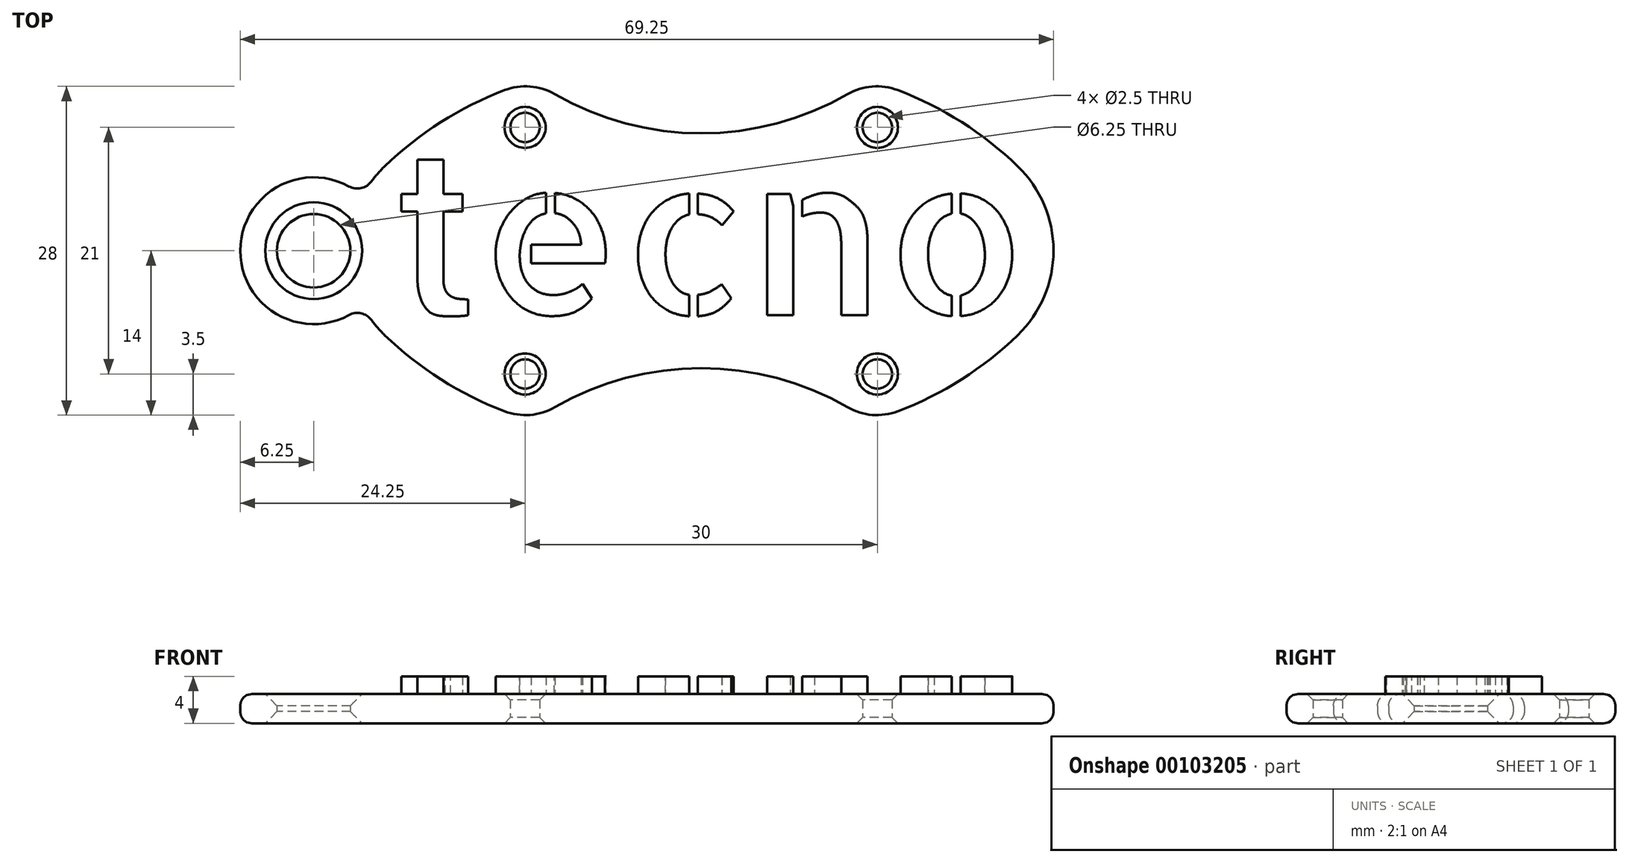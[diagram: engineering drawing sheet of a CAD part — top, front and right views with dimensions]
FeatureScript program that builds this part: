
annotation { "Feature Type Name" : "Feature", "Feature Type Description" : "" }
export const myFeature = defineFeature(function(context is Context, id is Id, definition is map)
    precondition{}
    {
        {
            var Q0;
            Q0=qCreatedBy(makeId("Top.planeOp"),FACE);
            var sketch = newSketch(context, id + "F0", { "sketchPlane" : qUnion([Q0])});
            skArc(sketch, "E0", {"start": v(-53.9, 14.37) * mm, "mid": v(-55.07, 13.14) * mm, "end": v(-56.13, 11.82) * mm});
            skArc(sketch, "E1.MirrorC", {"start": v(53.9, 14.37) * mm, "mid": v(60, 0) * mm, "end": v(53.9, -14.37) * mm});
            skArc(sketch, "E2", {"start": v(-53.9, -14.37) * mm, "mid": v(-44.35, -21.9) * mm, "end": v(-33.48, -27.35) * mm});
            skArc(sketch, "E3", {"start": v(24.94, -26.66) * mm, "mid": v(0, -20) * mm, "end": v(-24.94, -26.66) * mm});
            skArc(sketch, "E4", {"start": v(-33.48, -27.35) * mm, "mid": v(-29.13, -27.97) * mm, "end": v(-24.94, -26.66) * mm});
            skPoint(sketch, "E5.orphan", {"position": v(0, -30) * mm});
            skArc(sketch, "E6.MirrorCS", {"start": v(33.48, -27.35) * mm, "mid": v(29.13, -27.97) * mm, "end": v(24.94, -26.66) * mm});
            skArc(sketch, "E7.MirrorCS", {"start": v(53.9, -14.37) * mm, "mid": v(44.35, -21.9) * mm, "end": v(33.48, -27.35) * mm});
            skArc(sketch, "E8.MirrorCS", {"start": v(53.9, 14.37) * mm, "mid": v(44.35, 21.9) * mm, "end": v(33.48, 27.35) * mm});
            skArc(sketch, "E9.MirrorCS", {"start": v(33.48, 27.35) * mm, "mid": v(29.13, 27.97) * mm, "end": v(24.94, 26.66) * mm});
            skArc(sketch, "E10.MirrorCS", {"start": v(24.94, 26.66) * mm, "mid": v(0, 20) * mm, "end": v(-24.94, 26.66) * mm});
            skArc(sketch, "E11.MirrorCS", {"start": v(-33.48, 27.35) * mm, "mid": v(-29.13, 27.97) * mm, "end": v(-24.94, 26.66) * mm});
            skArc(sketch, "E12.MirrorCS", {"start": v(-53.9, 14.37) * mm, "mid": v(-44.35, 21.9) * mm, "end": v(-33.48, 27.35) * mm});
            skArc(sketch, "E13", {"start": v(-60, 10.96) * mm, "mid": v(-78.5, 0) * mm, "end": v(-60, -10.96) * mm});
            skArc(sketch, "E14.trimOffspring", {"start": v(-56.13, -11.82) * mm, "mid": v(-55.07, -13.14) * mm, "end": v(-53.9, -14.37) * mm});
            skArc(sketch, "E15", {"start": v(-60, 10.96) * mm, "mid": v(-57.9, 10.67) * mm, "end": v(-56.13, 11.82) * mm});
            skArc(sketch, "E16.MirrorCS", {"start": v(-60, -10.96) * mm, "mid": v(-57.9, -10.67) * mm, "end": v(-56.13, -11.82) * mm});
            skCircle(sketch, "E17", {"center": v(-66, 0) * mm, "radius": 6.25 * mm});
            skCircle(sketch, "E18", {"center": v(-30, -21) * mm, "radius": 2.5 * mm});
            skText(sketch, "E19", { "text": "tecno", "fontName": "AllertaStencil-Regular.ttf"});
            skCircle(sketch, "E20.MirrorC", {"center": v(-30, 21) * mm, "radius": 2.5 * mm});
            skCircle(sketch, "E21.MirrorC", {"center": v(30, 21) * mm, "radius": 2.5 * mm});
            skCircle(sketch, "E22.MirrorC", {"center": v(30, -21) * mm, "radius": 2.5 * mm});
            const initialGuessF0  = {"E19": [-0.05296, -0.011, 1, 0, 0.027]};
            skSetInitialGuess(sketch, initialGuessF0);
            skSolve(sketch);
        }
        {
            var Q0;
            Q0=makeQuery(id+"F0.imprint","IMPRINT",FACE,{"disambiguationData":[TD([[makeQuery(id+"F0.imprint","IMPRINT",EDGE,{"derivedFrom":sQuery(id+"F0.wireOp",EDGE,"E0")}),1.0]])]});
            extrude(context, id + "F1", {"entities" : qUnion([Q0]), "depth" : 5 * mm});
        }
        {
            var Q0;
            Q0=makeQuery(id+"F1.opExtrude","CAP_EDGE",EDGE,{"disambiguationData":[OSD([sQuery(id+"F0.wireOp",EDGE,"3ecefedf-33f3-4cd3-ba5f-a2dd52aaf8ab1.MirrorC")])],"isStart":true});
            var Q1;
            Q1=makeQuery(id+"F1.opExtrude","CAP_EDGE",EDGE,{"disambiguationData":[OSD([sQuery(id+"F0.wireOp",EDGE,"E20.MirrorC")])],"isStart":false});
            var Q2;
            Q2=makeQuery(id+"F1.opExtrude","CAP_EDGE",EDGE,{"disambiguationData":[OSD([sQuery(id+"F0.wireOp",EDGE,"E18")])],"isStart":false});
            var Q3;
            Q3=makeQuery(id+"F1.opExtrude","CAP_EDGE",EDGE,{"disambiguationData":[OSD([sQuery(id+"F0.wireOp",EDGE,"E22.MirrorC")])],"isStart":false});
            var Q4;
            Q4=makeQuery(id+"F1.opExtrude","CAP_EDGE",EDGE,{"disambiguationData":[OSD([sQuery(id+"F0.wireOp",EDGE,"E21.MirrorC")])],"isStart":false});
            var Q5;
            Q5=makeQuery(id+"F1.opExtrude","CAP_EDGE",EDGE,{"disambiguationData":[OSD([sQuery(id+"F0.wireOp",EDGE,"E21.MirrorC")])],"isStart":true});
            var Q6;
            Q6=makeQuery(id+"F1.opExtrude","CAP_EDGE",EDGE,{"disambiguationData":[OSD([sQuery(id+"F0.wireOp",EDGE,"E22.MirrorC")])],"isStart":true});
            var Q7;
            Q7=makeQuery(id+"F1.opExtrude","CAP_EDGE",EDGE,{"disambiguationData":[OSD([sQuery(id+"F0.wireOp",EDGE,"E18")])],"isStart":true});
            var Q8;
            Q8=makeQuery(id+"F1.opExtrude","CAP_EDGE",EDGE,{"disambiguationData":[OSD([sQuery(id+"F0.wireOp",EDGE,"E20.MirrorC")])],"isStart":true});
            chamfer(context, id + "F2", {"entities" : qUnion([Q0, Q1, Q2, Q3, Q4, Q5, Q6, Q7, Q8]), "width" : 1 * mm, "tangentPropagation" : true});
        }
        {
            var Q0;
            Q0=makeQuery(id+"F1.opExtrude","CAP_EDGE",EDGE,{"disambiguationData":[OSD([sQuery(id+"F0.wireOp",EDGE,"E17")])],"isStart":false});
            var Q1;
            Q1=makeQuery(id+"F1.opExtrude","CAP_EDGE",EDGE,{"disambiguationData":[OSD([sQuery(id+"F0.wireOp",EDGE,"E17")])],"isStart":true});
            chamfer(context, id + "F3", {"entities" : qUnion([Q0, Q1]), "width" : 2 * mm, "tangentPropagation" : true});
        }
        {
            var Q0;
            Q0=makeQuery(id+"F1.opExtrude","CAP_EDGE",EDGE,{"disambiguationData":[OSD([sQuery(id+"F0.wireOp",EDGE,"E3")])],"isStart":false});
            var Q1;
            Q1=makeQuery(id+"F1.opExtrude","CAP_EDGE",EDGE,{"disambiguationData":[OSD([sQuery(id+"F0.wireOp",EDGE,"E7.MirrorCS")])],"isStart":true});
            fillet(context, id + "F4", {"entities" : qUnion([Q0, Q1]), "radius" : 2 * mm, "tangentPropagation" : true, "allowEdgeOverflow" : false});
        }
        {
            var Q0;
            Q0=makeQuery(id+"F0.imprint","IMPRINT",FACE,{"disambiguationData":[TD([[makeQuery(id+"F0.imprint","IMPRINT",EDGE,{"derivedFrom":sQuery(id+"F0.wireOp",EDGE,"E19.sketch_text.stroke-0")}),-1.0]])]});
            var Q1;
            Q1=makeQuery(id+"F0.imprint","IMPRINT",FACE,{"disambiguationData":[TD([[makeQuery(id+"F0.imprint","IMPRINT",EDGE,{"derivedFrom":sQuery(id+"F0.wireOp",EDGE,"E19.sketch_text.stroke-38")}),-1.0]])]});
            var Q2;
            Q2=makeQuery(id+"F0.imprint","IMPRINT",FACE,{"disambiguationData":[TD([[makeQuery(id+"F0.imprint","IMPRINT",EDGE,{"derivedFrom":sQuery(id+"F0.wireOp",EDGE,"E19.sketch_text.stroke-25")}),-1.0]])]});
            var Q3;
            Q3=makeQuery(id+"F0.imprint","IMPRINT",FACE,{"disambiguationData":[TD([[makeQuery(id+"F0.imprint","IMPRINT",EDGE,{"derivedFrom":sQuery(id+"F0.wireOp",EDGE,"E19.sketch_text.stroke-74")}),-1.0]])]});
            var Q4;
            Q4=makeQuery(id+"F0.imprint","IMPRINT",FACE,{"disambiguationData":[TD([[makeQuery(id+"F0.imprint","IMPRINT",EDGE,{"derivedFrom":sQuery(id+"F0.wireOp",EDGE,"E19.sketch_text.stroke-90")}),-1.0]])]});
            var Q5;
            Q5=makeQuery(id+"F0.imprint","IMPRINT",FACE,{"disambiguationData":[TD([[makeQuery(id+"F0.imprint","IMPRINT",EDGE,{"derivedFrom":sQuery(id+"F0.wireOp",EDGE,"E19.sketch_text.stroke-62")}),-1.0]])]});
            var Q6;
            Q6=makeQuery(id+"F0.imprint","IMPRINT",FACE,{"disambiguationData":[TD([[makeQuery(id+"F0.imprint","IMPRINT",EDGE,{"derivedFrom":sQuery(id+"F0.wireOp",EDGE,"E19.sketch_text.stroke-95")}),-1.0]])]});
            var Q7;
            Q7=makeQuery(id+"F0.imprint","IMPRINT",FACE,{"disambiguationData":[TD([[makeQuery(id+"F0.imprint","IMPRINT",EDGE,{"derivedFrom":sQuery(id+"F0.wireOp",EDGE,"E19.sketch_text.stroke-130")}),-1.0]])]});
            var Q8;
            Q8=makeQuery(id+"F0.imprint","IMPRINT",FACE,{"disambiguationData":[TD([[makeQuery(id+"F0.imprint","IMPRINT",EDGE,{"derivedFrom":sQuery(id+"F0.wireOp",EDGE,"E19.sketch_text.stroke-114")}),-1.0]])]});
            var Q9;
            Q9=makeQuery(id+"F0.imprint","IMPRINT",FACE,{"disambiguationData":[TD([[makeQuery(id+"F0.imprint","IMPRINT",EDGE,{"derivedFrom":sQuery(id+"F0.wireOp",EDGE,"E19.sketch_text.stroke-68")}),-1.0]])]});
            extrude(context, id + "F5", {"entities" : qUnion([Q0, Q1, Q2, Q3, Q4, Q5, Q6, Q7, Q8, Q9]), "operationType" : NewBodyOperationType.ADD, "depth" : 8 * mm});
        }
        {
            var Q0;
            Q0=makeQuery(id+"F1.opExtrude","SWEPT_BODY",BODY,{"disambiguationData":[OSD([sQuery(id+"F0.wireOp",EDGE,"E0"),sQuery(id+"F0.wireOp",EDGE,"E1.MirrorC"),sQuery(id+"F0.wireOp",EDGE,"E2"),sQuery(id+"F0.wireOp",EDGE,"E3"),sQuery(id+"F0.wireOp",EDGE,"E4"),sQuery(id+"F0.wireOp",EDGE,"E6.MirrorCS"),sQuery(id+"F0.wireOp",EDGE,"E7.MirrorCS"),sQuery(id+"F0.wireOp",EDGE,"E8.MirrorCS"),sQuery(id+"F0.wireOp",EDGE,"E9.MirrorCS"),sQuery(id+"F0.wireOp",EDGE,"E10.MirrorCS"),sQuery(id+"F0.wireOp",EDGE,"E11.MirrorCS"),sQuery(id+"F0.wireOp",EDGE,"E12.MirrorCS"),sQuery(id+"F0.wireOp",EDGE,"E13"),sQuery(id+"F0.wireOp",EDGE,"E14.trimOffspring"),sQuery(id+"F0.wireOp",EDGE,"E15"),sQuery(id+"F0.wireOp",EDGE,"E16.MirrorCS"),sQuery(id+"F0.wireOp",EDGE,"E17"),sQuery(id+"F0.wireOp",EDGE,"E18"),sQuery(id+"F0.wireOp",EDGE,"E19.sketch_text.stroke-0"),sQuery(id+"F0.wireOp",EDGE,"E19.sketch_text.stroke-1"),sQuery(id+"F0.wireOp",EDGE,"E19.sketch_text.stroke-2"),sQuery(id+"F0.wireOp",EDGE,"E19.sketch_text.stroke-3"),sQuery(id+"F0.wireOp",EDGE,"E19.sketch_text.stroke-4"),sQuery(id+"F0.wireOp",EDGE,"E19.sketch_text.stroke-5"),sQuery(id+"F0.wireOp",EDGE,"E19.sketch_text.stroke-6"),sQuery(id+"F0.wireOp",EDGE,"E19.sketch_text.stroke-7"),sQuery(id+"F0.wireOp",EDGE,"E19.sketch_text.stroke-8"),sQuery(id+"F0.wireOp",EDGE,"E19.sketch_text.stroke-9"),sQuery(id+"F0.wireOp",EDGE,"E19.sketch_text.stroke-10"),sQuery(id+"F0.wireOp",EDGE,"E19.sketch_text.stroke-11"),sQuery(id+"F0.wireOp",EDGE,"E19.sketch_text.stroke-12"),sQuery(id+"F0.wireOp",EDGE,"E19.sketch_text.stroke-13"),sQuery(id+"F0.wireOp",EDGE,"E19.sketch_text.stroke-14"),sQuery(id+"F0.wireOp",EDGE,"E19.sketch_text.stroke-15"),sQuery(id+"F0.wireOp",EDGE,"E19.sketch_text.stroke-16"),sQuery(id+"F0.wireOp",EDGE,"E19.sketch_text.stroke-17"),sQuery(id+"F0.wireOp",EDGE,"E19.sketch_text.stroke-18"),sQuery(id+"F0.wireOp",EDGE,"E19.sketch_text.stroke-19"),sQuery(id+"F0.wireOp",EDGE,"E19.sketch_text.stroke-20"),sQuery(id+"F0.wireOp",EDGE,"E19.sketch_text.stroke-21"),sQuery(id+"F0.wireOp",EDGE,"E19.sketch_text.stroke-22"),sQuery(id+"F0.wireOp",EDGE,"E19.sketch_text.stroke-23"),sQuery(id+"F0.wireOp",EDGE,"E19.sketch_text.stroke-24"),sQuery(id+"F0.wireOp",EDGE,"E19.sketch_text.stroke-25"),sQuery(id+"F0.wireOp",EDGE,"E19.sketch_text.stroke-26"),sQuery(id+"F0.wireOp",EDGE,"E19.sketch_text.stroke-27"),sQuery(id+"F0.wireOp",EDGE,"E19.sketch_text.stroke-28"),sQuery(id+"F0.wireOp",EDGE,"E19.sketch_text.stroke-29"),sQuery(id+"F0.wireOp",EDGE,"E19.sketch_text.stroke-30"),sQuery(id+"F0.wireOp",EDGE,"E19.sketch_text.stroke-31"),sQuery(id+"F0.wireOp",EDGE,"E19.sketch_text.stroke-32"),sQuery(id+"F0.wireOp",EDGE,"E19.sketch_text.stroke-33"),sQuery(id+"F0.wireOp",EDGE,"E19.sketch_text.stroke-34"),sQuery(id+"F0.wireOp",EDGE,"E19.sketch_text.stroke-35"),sQuery(id+"F0.wireOp",EDGE,"E19.sketch_text.stroke-36"),sQuery(id+"F0.wireOp",EDGE,"E19.sketch_text.stroke-37"),sQuery(id+"F0.wireOp",EDGE,"E19.sketch_text.stroke-38"),sQuery(id+"F0.wireOp",EDGE,"E19.sketch_text.stroke-39"),sQuery(id+"F0.wireOp",EDGE,"E19.sketch_text.stroke-40"),sQuery(id+"F0.wireOp",EDGE,"E19.sketch_text.stroke-41"),sQuery(id+"F0.wireOp",EDGE,"E19.sketch_text.stroke-42"),sQuery(id+"F0.wireOp",EDGE,"E19.sketch_text.stroke-43"),sQuery(id+"F0.wireOp",EDGE,"E19.sketch_text.stroke-44"),sQuery(id+"F0.wireOp",EDGE,"E19.sketch_text.stroke-45"),sQuery(id+"F0.wireOp",EDGE,"E19.sketch_text.stroke-46"),sQuery(id+"F0.wireOp",EDGE,"E19.sketch_text.stroke-47"),sQuery(id+"F0.wireOp",EDGE,"E19.sketch_text.stroke-48"),sQuery(id+"F0.wireOp",EDGE,"E19.sketch_text.stroke-49"),sQuery(id+"F0.wireOp",EDGE,"E19.sketch_text.stroke-50"),sQuery(id+"F0.wireOp",EDGE,"E19.sketch_text.stroke-51"),sQuery(id+"F0.wireOp",EDGE,"E19.sketch_text.stroke-52"),sQuery(id+"F0.wireOp",EDGE,"E19.sketch_text.stroke-53"),sQuery(id+"F0.wireOp",EDGE,"E19.sketch_text.stroke-54"),sQuery(id+"F0.wireOp",EDGE,"E19.sketch_text.stroke-55"),sQuery(id+"F0.wireOp",EDGE,"E19.sketch_text.stroke-56"),sQuery(id+"F0.wireOp",EDGE,"E19.sketch_text.stroke-57"),sQuery(id+"F0.wireOp",EDGE,"E19.sketch_text.stroke-58"),sQuery(id+"F0.wireOp",EDGE,"E19.sketch_text.stroke-59"),sQuery(id+"F0.wireOp",EDGE,"E19.sketch_text.stroke-60"),sQuery(id+"F0.wireOp",EDGE,"E19.sketch_text.stroke-61"),sQuery(id+"F0.wireOp",EDGE,"E19.sketch_text.stroke-62"),sQuery(id+"F0.wireOp",EDGE,"E19.sketch_text.stroke-63"),sQuery(id+"F0.wireOp",EDGE,"E19.sketch_text.stroke-64"),sQuery(id+"F0.wireOp",EDGE,"E19.sketch_text.stroke-65"),sQuery(id+"F0.wireOp",EDGE,"E19.sketch_text.stroke-66"),sQuery(id+"F0.wireOp",EDGE,"E19.sketch_text.stroke-67"),sQuery(id+"F0.wireOp",EDGE,"E19.sketch_text.stroke-68"),sQuery(id+"F0.wireOp",EDGE,"E19.sketch_text.stroke-69"),sQuery(id+"F0.wireOp",EDGE,"E19.sketch_text.stroke-70"),sQuery(id+"F0.wireOp",EDGE,"E19.sketch_text.stroke-71"),sQuery(id+"F0.wireOp",EDGE,"E19.sketch_text.stroke-72"),sQuery(id+"F0.wireOp",EDGE,"E19.sketch_text.stroke-73"),sQuery(id+"F0.wireOp",EDGE,"E19.sketch_text.stroke-74"),sQuery(id+"F0.wireOp",EDGE,"E19.sketch_text.stroke-75"),sQuery(id+"F0.wireOp",EDGE,"E19.sketch_text.stroke-76"),sQuery(id+"F0.wireOp",EDGE,"E19.sketch_text.stroke-77"),sQuery(id+"F0.wireOp",EDGE,"E19.sketch_text.stroke-78"),sQuery(id+"F0.wireOp",EDGE,"E19.sketch_text.stroke-79"),sQuery(id+"F0.wireOp",EDGE,"E19.sketch_text.stroke-80"),sQuery(id+"F0.wireOp",EDGE,"E19.sketch_text.stroke-81"),sQuery(id+"F0.wireOp",EDGE,"E19.sketch_text.stroke-82"),sQuery(id+"F0.wireOp",EDGE,"E19.sketch_text.stroke-83"),sQuery(id+"F0.wireOp",EDGE,"E19.sketch_text.stroke-84"),sQuery(id+"F0.wireOp",EDGE,"E19.sketch_text.stroke-85"),sQuery(id+"F0.wireOp",EDGE,"E19.sketch_text.stroke-86"),sQuery(id+"F0.wireOp",EDGE,"E19.sketch_text.stroke-87"),sQuery(id+"F0.wireOp",EDGE,"E19.sketch_text.stroke-88"),sQuery(id+"F0.wireOp",EDGE,"E19.sketch_text.stroke-89"),sQuery(id+"F0.wireOp",EDGE,"E19.sketch_text.stroke-90"),sQuery(id+"F0.wireOp",EDGE,"E19.sketch_text.stroke-91"),sQuery(id+"F0.wireOp",EDGE,"E19.sketch_text.stroke-92"),sQuery(id+"F0.wireOp",EDGE,"E19.sketch_text.stroke-93"),sQuery(id+"F0.wireOp",EDGE,"E19.sketch_text.stroke-94"),sQuery(id+"F0.wireOp",EDGE,"E19.sketch_text.stroke-95"),sQuery(id+"F0.wireOp",EDGE,"E19.sketch_text.stroke-96"),sQuery(id+"F0.wireOp",EDGE,"E19.sketch_text.stroke-97"),sQuery(id+"F0.wireOp",EDGE,"E19.sketch_text.stroke-98"),sQuery(id+"F0.wireOp",EDGE,"E19.sketch_text.stroke-99"),sQuery(id+"F0.wireOp",EDGE,"E19.sketch_text.stroke-100"),sQuery(id+"F0.wireOp",EDGE,"E19.sketch_text.stroke-101"),sQuery(id+"F0.wireOp",EDGE,"E19.sketch_text.stroke-102"),sQuery(id+"F0.wireOp",EDGE,"E19.sketch_text.stroke-103"),sQuery(id+"F0.wireOp",EDGE,"E19.sketch_text.stroke-104"),sQuery(id+"F0.wireOp",EDGE,"E19.sketch_text.stroke-105"),sQuery(id+"F0.wireOp",EDGE,"E19.sketch_text.stroke-106"),sQuery(id+"F0.wireOp",EDGE,"E19.sketch_text.stroke-107"),sQuery(id+"F0.wireOp",EDGE,"E19.sketch_text.stroke-108"),sQuery(id+"F0.wireOp",EDGE,"E19.sketch_text.stroke-109"),sQuery(id+"F0.wireOp",EDGE,"E19.sketch_text.stroke-110"),sQuery(id+"F0.wireOp",EDGE,"E19.sketch_text.stroke-111"),sQuery(id+"F0.wireOp",EDGE,"E19.sketch_text.stroke-112"),sQuery(id+"F0.wireOp",EDGE,"E19.sketch_text.stroke-113"),sQuery(id+"F0.wireOp",EDGE,"E19.sketch_text.stroke-114"),sQuery(id+"F0.wireOp",EDGE,"E19.sketch_text.stroke-115"),sQuery(id+"F0.wireOp",EDGE,"E19.sketch_text.stroke-116"),sQuery(id+"F0.wireOp",EDGE,"E19.sketch_text.stroke-117"),sQuery(id+"F0.wireOp",EDGE,"E19.sketch_text.stroke-118"),sQuery(id+"F0.wireOp",EDGE,"E19.sketch_text.stroke-119"),sQuery(id+"F0.wireOp",EDGE,"E19.sketch_text.stroke-120"),sQuery(id+"F0.wireOp",EDGE,"E19.sketch_text.stroke-121"),sQuery(id+"F0.wireOp",EDGE,"E19.sketch_text.stroke-122"),sQuery(id+"F0.wireOp",EDGE,"E19.sketch_text.stroke-123"),sQuery(id+"F0.wireOp",EDGE,"E19.sketch_text.stroke-124"),sQuery(id+"F0.wireOp",EDGE,"E19.sketch_text.stroke-125"),sQuery(id+"F0.wireOp",EDGE,"E19.sketch_text.stroke-126"),sQuery(id+"F0.wireOp",EDGE,"E19.sketch_text.stroke-127"),sQuery(id+"F0.wireOp",EDGE,"E19.sketch_text.stroke-128"),sQuery(id+"F0.wireOp",EDGE,"E19.sketch_text.stroke-129"),sQuery(id+"F0.wireOp",EDGE,"E19.sketch_text.stroke-130"),sQuery(id+"F0.wireOp",EDGE,"E19.sketch_text.stroke-131"),sQuery(id+"F0.wireOp",EDGE,"E19.sketch_text.stroke-132"),sQuery(id+"F0.wireOp",EDGE,"E19.sketch_text.stroke-133"),sQuery(id+"F0.wireOp",EDGE,"E19.sketch_text.stroke-134"),sQuery(id+"F0.wireOp",EDGE,"E19.sketch_text.stroke-135"),sQuery(id+"F0.wireOp",EDGE,"E19.sketch_text.stroke-136"),sQuery(id+"F0.wireOp",EDGE,"E19.sketch_text.stroke-137"),sQuery(id+"F0.wireOp",EDGE,"E19.sketch_text.stroke-138"),sQuery(id+"F0.wireOp",EDGE,"E19.sketch_text.stroke-139"),sQuery(id+"F0.wireOp",EDGE,"E19.sketch_text.stroke-140"),sQuery(id+"F0.wireOp",EDGE,"E19.sketch_text.stroke-141"),sQuery(id+"F0.wireOp",EDGE,"E19.sketch_text.stroke-142"),sQuery(id+"F0.wireOp",EDGE,"E19.sketch_text.stroke-143"),sQuery(id+"F0.wireOp",EDGE,"E19.sketch_text.stroke-144"),sQuery(id+"F0.wireOp",EDGE,"E19.sketch_text.stroke-145"),sQuery(id+"F0.wireOp",EDGE,"E20.MirrorC"),sQuery(id+"F0.wireOp",EDGE,"E21.MirrorC"),sQuery(id+"F0.wireOp",EDGE,"E22.MirrorC")])]});
            var Q1;
            Q1=qCreatedBy(makeId("Origin.pointOp"),VERTEX);
            transform(context, id + "F6", {"entities" : qUnion([Q0]), "transformType" : TransformType.SCALE_UNIFORMLY, "scale" : 0.5, "scalePoint" : qUnion([Q1]), "makeCopy" : false});
        }
    });
